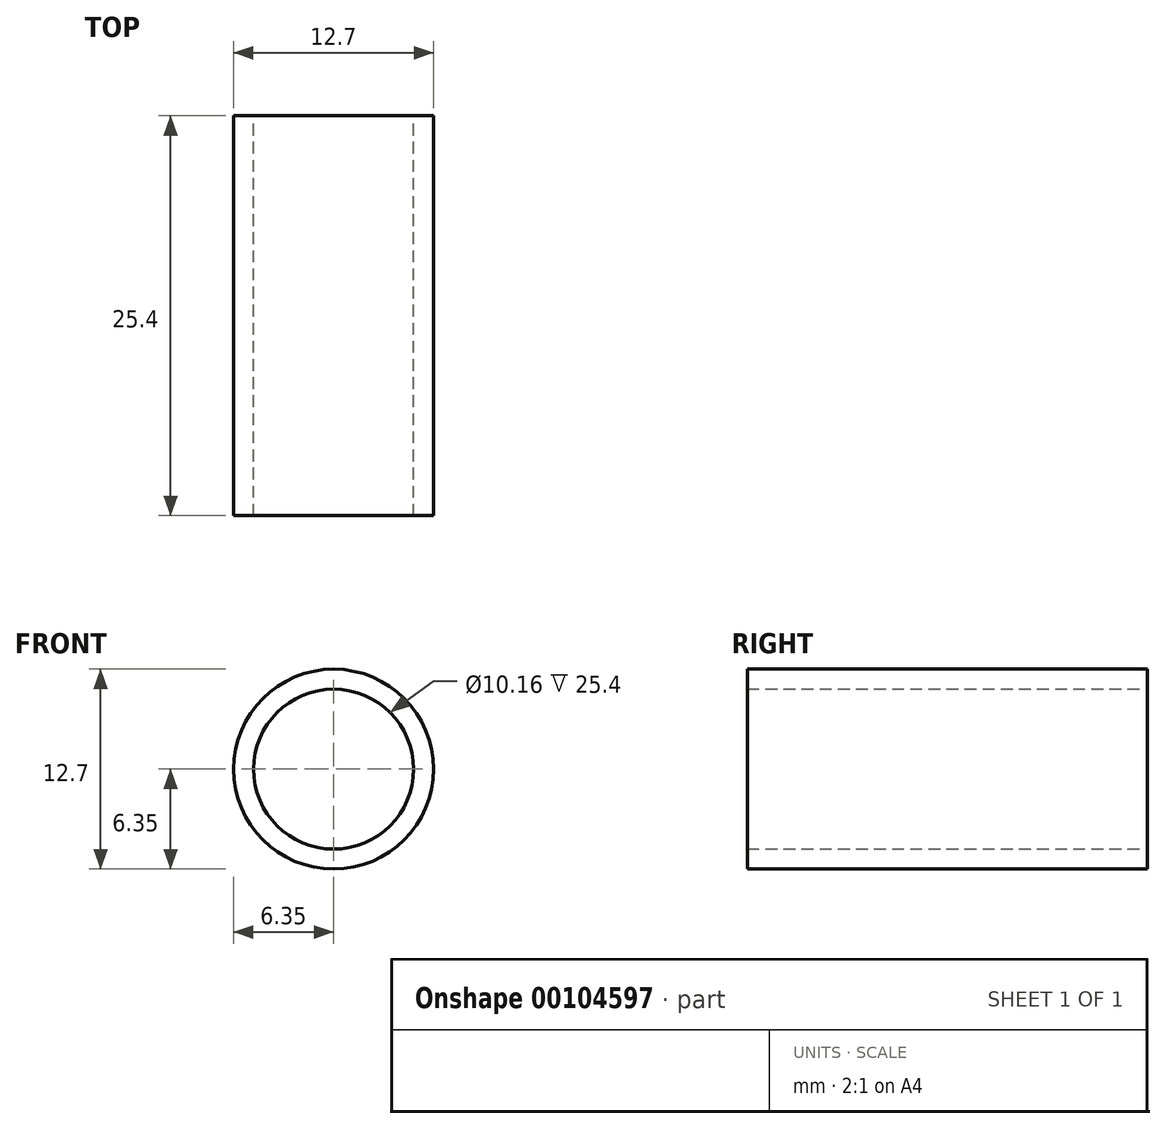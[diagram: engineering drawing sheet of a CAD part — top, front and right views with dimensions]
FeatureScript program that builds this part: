
annotation { "Feature Type Name" : "Feature", "Feature Type Description" : "" }
export const myFeature = defineFeature(function(context is Context, id is Id, definition is map)
    precondition{}
    {
        {
            var Q0;
            Q0=qCreatedBy(makeId("Front.planeOp"),FACE);
            var sketch = newSketch(context, id + "F0", { "sketchPlane" : qUnion([Q0])});
            skCircle(sketch, "E0", {"center": v(0, 0) * mm, "radius": 6.35 * mm});
            skCircle(sketch, "E1", {"center": v(0, 0) * mm, "radius": 5.08 * mm});
            skSolve(sketch);
        }
        {
            var Q0;
            Q0=qCreatedBy(makeId("Right.planeOp"),FACE);
            var sketch = newSketch(context, id + "F1", { "sketchPlane" : qUnion([Q0])});
            skLineSegment(sketch, "E2", {"start": v(0, 0) * mm, "end": v(25.4, 0) * mm});
            skSolve(sketch);
        }
        {
            var Q0;
            Q0=makeQuery(id+"F0.imprint","IMPRINT",FACE,{"disambiguationData":[TD([[makeQuery(id+"F0.imprint","IMPRINT",EDGE,{"derivedFrom":sQuery(id+"F0.wireOp",EDGE,"E0")}),1.0]])]});
            var Q1;
            Q1=sQuery(id+"F1.wireOp",EDGE,"E2");
            sweep(context, id + "F2", {"profiles" : qUnion([Q0]), "path" : qUnion([Q1])});
        }
    });
